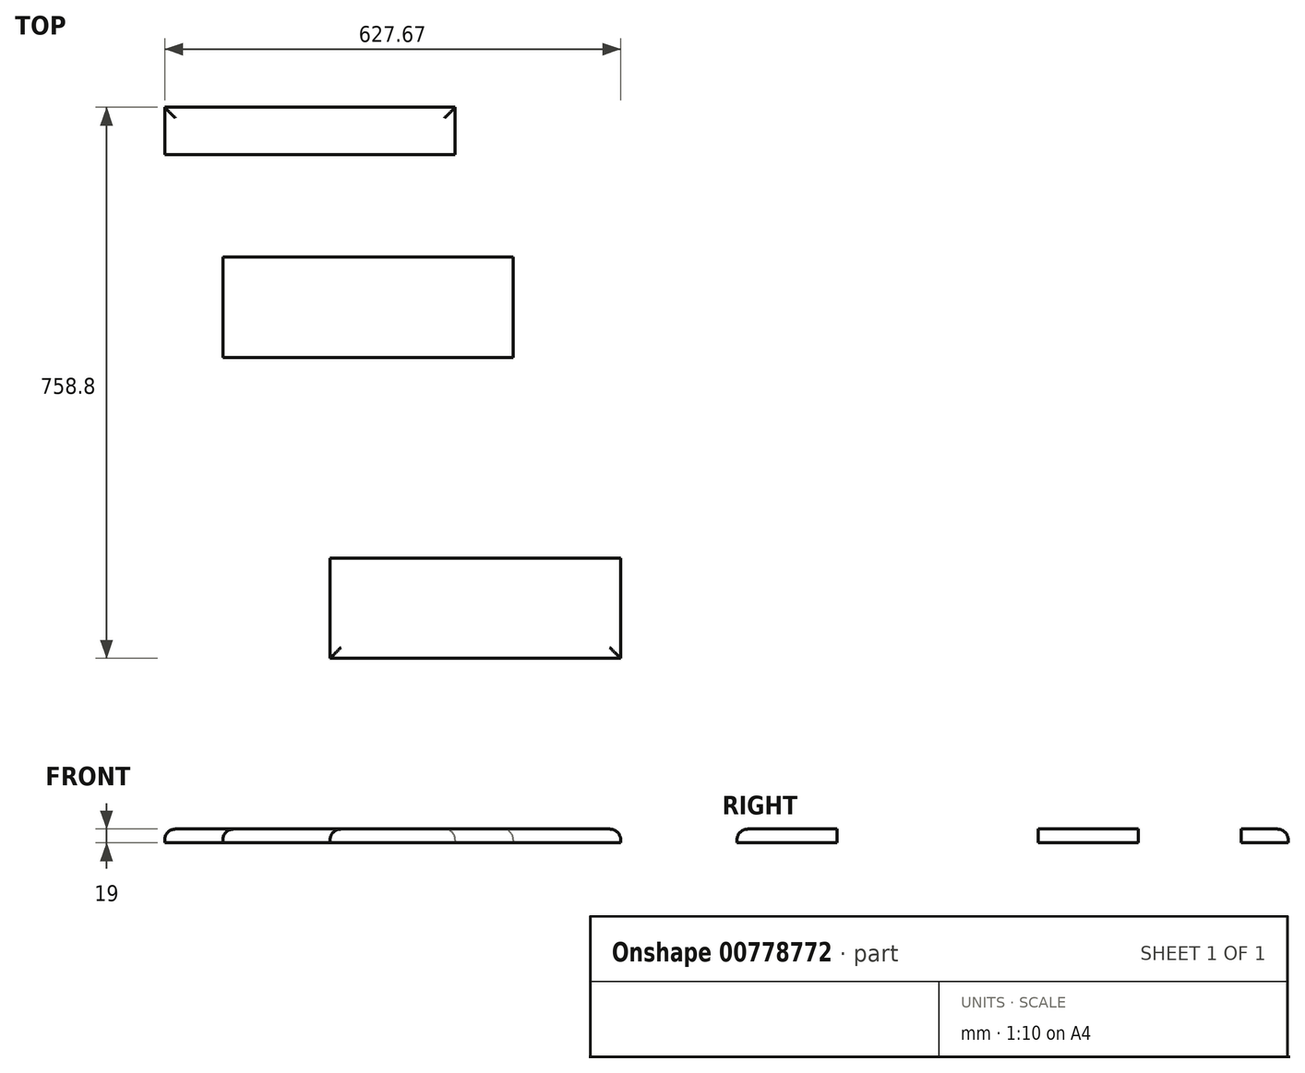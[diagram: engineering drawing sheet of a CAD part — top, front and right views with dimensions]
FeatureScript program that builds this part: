
annotation { "Feature Type Name" : "Feature", "Feature Type Description" : "" }
export const myFeature = defineFeature(function(context is Context, id is Id, definition is map)
    precondition{}
    {
        {
            var Q0;
            Q0=qCreatedBy(makeId("Top.planeOp"),FACE);
            var sketch = newSketch(context, id + "F0", { "sketchPlane" : qUnion([Q0])});
            skLineSegment(sketch, "E0.bottom", {"start": v(-200, 96.98) * mm, "end": v(200, 96.98) * mm});
            skLineSegment(sketch, "E0.top", {"start": v(-200, -41.02) * mm, "end": v(200, -41.02) * mm});
            skLineSegment(sketch, "E0.left", {"start": v(-200, 96.98) * mm, "end": v(-200, -41.02) * mm});
            skLineSegment(sketch, "E0.right", {"start": v(200, 96.98) * mm, "end": v(200, -41.02) * mm});
            skPoint(sketch, "E0.middle", {"position": v(0, 27.98) * mm});
            skLineSegment(sketch, "E1.bottom", {"start": v(-52.31, -317.42) * mm, "end": v(347.69, -317.42) * mm});
            skLineSegment(sketch, "E1.top", {"start": v(-52.31, -455.42) * mm, "end": v(347.69, -455.42) * mm});
            skLineSegment(sketch, "E1.left", {"start": v(-52.31, -317.42) * mm, "end": v(-52.31, -455.42) * mm});
            skLineSegment(sketch, "E1.right", {"start": v(347.69, -317.42) * mm, "end": v(347.69, -455.42) * mm});
            skPoint(sketch, "E1.middle", {"position": v(147.69, -386.42) * mm});
            skLineSegment(sketch, "E2.bottom", {"start": v(120.02, 303.38) * mm, "end": v(-279.98, 303.38) * mm});
            skLineSegment(sketch, "E2.top", {"start": v(120.02, 238.38) * mm, "end": v(-279.98, 238.38) * mm});
            skLineSegment(sketch, "E2.left", {"start": v(120.02, 303.38) * mm, "end": v(120.02, 238.38) * mm});
            skLineSegment(sketch, "E2.right", {"start": v(-279.98, 303.38) * mm, "end": v(-279.98, 238.38) * mm});
            skPoint(sketch, "E2.middle", {"position": v(-79.98, 270.88) * mm});
            skSolve(sketch);
        }
        {
            var Q0;
            Q0 = qSketchRegion(id + "F0", true);
            extrude(context, id + "F1", {"entities" : qUnion([Q0]), "depth" : 19 * mm, "offsetDistance" : 25 * mm});
        }
        {
            var Q0;
            Q0=makeQuery(id+"F1.opExtrude","CAP_EDGE",EDGE,{"disambiguationData":[OSD([sQuery(id+"F0.wireOp",EDGE,"E1.top")])],"isStart":false});
            var Q1;
            Q1=makeQuery(id+"F1.opExtrude","CAP_EDGE",EDGE,{"disambiguationData":[OSD([sQuery(id+"F0.wireOp",EDGE,"E1.left")])],"isStart":false});
            var Q2;
            Q2=makeQuery(id+"F1.opExtrude","CAP_EDGE",EDGE,{"disambiguationData":[OSD([sQuery(id+"F0.wireOp",EDGE,"E1.right")])],"isStart":false});
            var Q3;
            Q3=makeQuery(id+"F1.opExtrude","CAP_EDGE",EDGE,{"disambiguationData":[OSD([sQuery(id+"F0.wireOp",EDGE,"E0.right")])],"isStart":false});
            var Q4;
            Q4=makeQuery(id+"F1.opExtrude","CAP_EDGE",EDGE,{"disambiguationData":[OSD([sQuery(id+"F0.wireOp",EDGE,"E0.left")])],"isStart":false});
            var Q5;
            Q5=makeQuery(id+"F1.opExtrude","CAP_EDGE",EDGE,{"disambiguationData":[OSD([sQuery(id+"F0.wireOp",EDGE,"E2.right")])],"isStart":false});
            var Q6;
            Q6=makeQuery(id+"F1.opExtrude","CAP_EDGE",EDGE,{"disambiguationData":[OSD([sQuery(id+"F0.wireOp",EDGE,"E2.bottom")])],"isStart":false});
            var Q7;
            Q7=makeQuery(id+"F1.opExtrude","CAP_EDGE",EDGE,{"disambiguationData":[OSD([sQuery(id+"F0.wireOp",EDGE,"E2.left")])],"isStart":false});
            fillet(context, id + "F2", {"entities" : qUnion([Q0, Q1, Q2, Q3, Q4, Q5, Q6, Q7]), "radius" : 15 * mm, "tangentPropagation" : true, "allowEdgeOverflow" : false});
        }
    });
